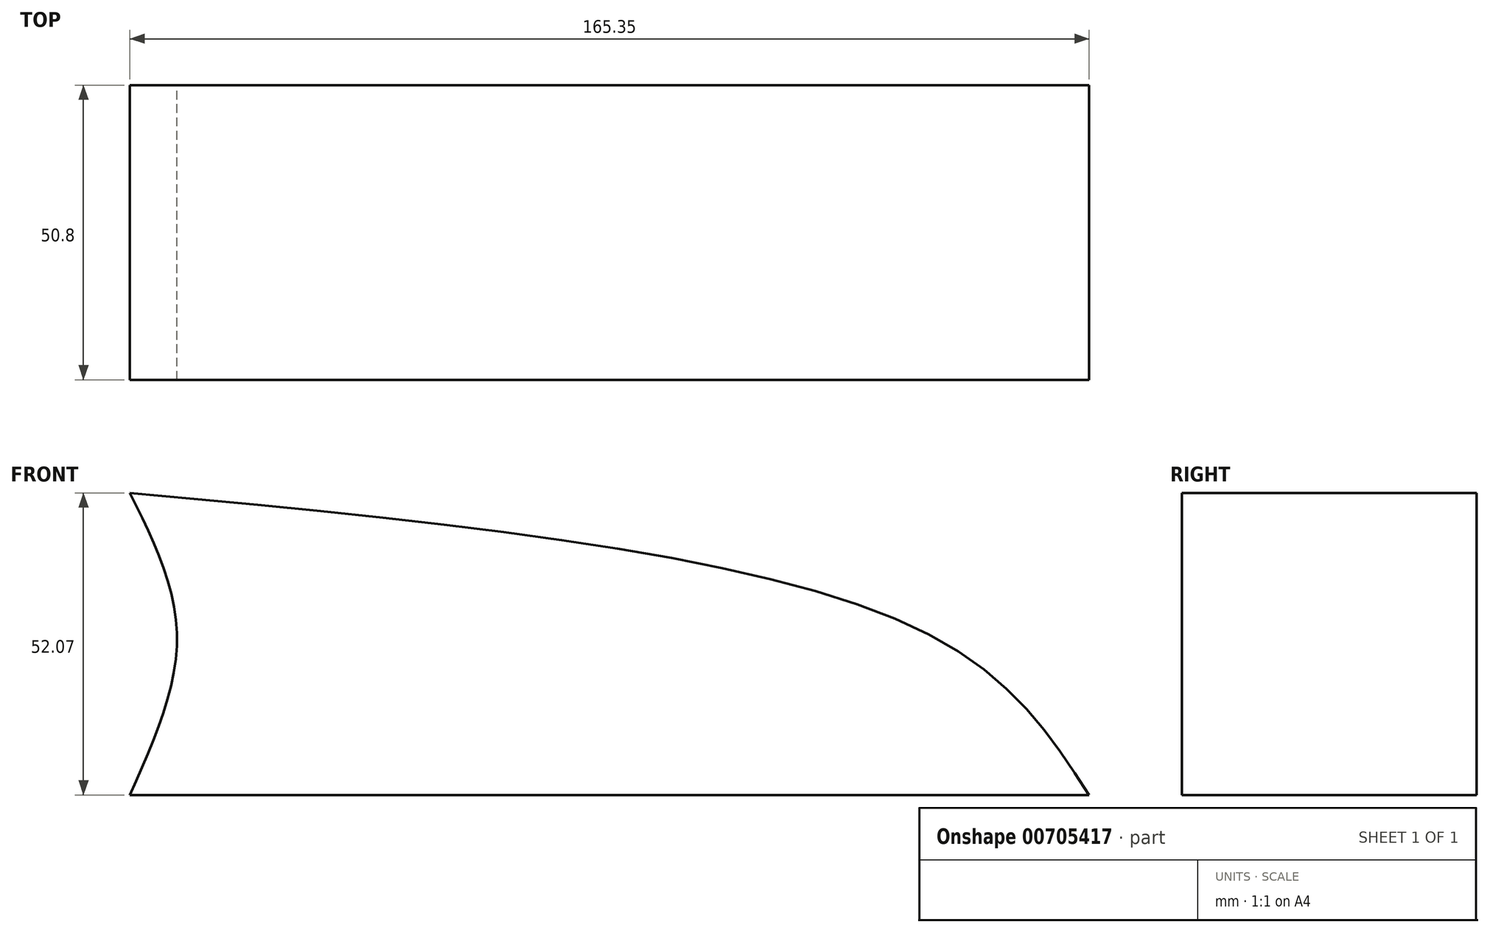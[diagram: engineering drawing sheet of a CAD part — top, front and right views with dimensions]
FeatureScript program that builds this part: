
annotation { "Feature Type Name" : "Feature", "Feature Type Description" : "" }
export const myFeature = defineFeature(function(context is Context, id is Id, definition is map)
    precondition{}
    {
        {
            var Q0;
            Q0=qCreatedBy(makeId("Front.planeOp"),FACE);
            var sketch = newSketch(context, id + "F0", { "sketchPlane" : qUnion([Q0])});
            skLineSegment(sketch, "E0", {"start": v(-84.2, -42.04) * mm, "end": v(81.15, -42.04) * mm});
            skFitSpline(sketch, "E1", {"points": [v(-84.2, 10.03) * mm, v(53.98, -14.6) * mm, v(81.15, -42.04) * mm], "startDerivative": vector(253.83, -23.73) * mm, "endDerivative": vector(56.34, -86.99) * mm});
            skFitSpline(sketch, "E2", {"points": [v(-84.2, 10.03) * mm, v(-76.07, -14.6) * mm, v(-84.2, -42.04) * mm], "startDerivative": vector(24.6, -49.77) * mm, "endDerivative": vector(-24.2, -54.33) * mm});
            skSolve(sketch);
        }
        {
            var Q0;
            Q0 = qSketchRegion(id + "F0", true);
            extrude(context, id + "F1", {"entities" : qUnion([Q0]), "depth" : 50.8 * mm, "offsetDistance" : 25.4 * mm});
        }
    });
